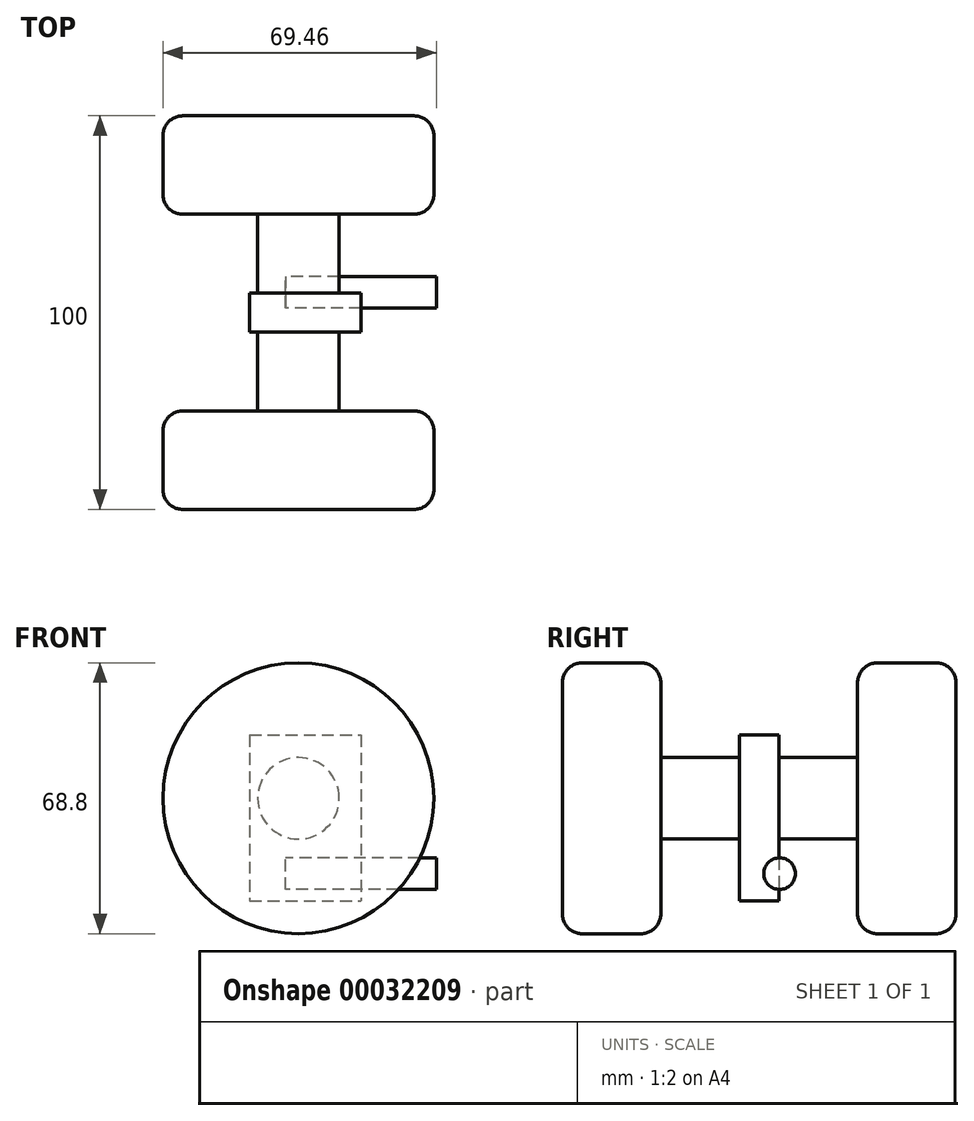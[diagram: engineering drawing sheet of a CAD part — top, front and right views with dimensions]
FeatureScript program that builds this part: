
annotation { "Feature Type Name" : "Feature", "Feature Type Description" : "" }
export const myFeature = defineFeature(function(context is Context, id is Id, definition is map)
    precondition{}
    {
        {
            var Q0;
            Q0=qCreatedBy(makeId("Front.planeOp"),FACE);
            var sketch = newSketch(context, id + "F0", { "sketchPlane" : qUnion([Q0])});
            skCircle(sketch, "E0", {"center": v(0, 0) * mm, "radius": 34.4 * mm});
            skSolve(sketch);
        }
        {
            var Q0;
            Q0=makeQuery(id+"F0.imprint","IMPRINT",FACE,{"disambiguationData":[TD([[makeQuery(id+"F0.imprint","IMPRINT",EDGE,{"derivedFrom":sQuery(id+"F0.wireOp",EDGE,"E0")}),1.0]])]});
            extrude(context, id + "F1", {"entities" : qUnion([Q0]), "depth" : 25 * mm});
        }
        {
            var Q0;
            Q0=makeQuery(id+"F1.opExtrude","CAP_FACE",FACE,{"disambiguationData":[OSD([sQuery(id+"F0.wireOp",EDGE,"E0")])],"isStart":true});
            var sketch = newSketch(context, id + "F2", { "sketchPlane" : qUnion([Q0])});
            skCircle(sketch, "E1", {"center": v(0, 0) * mm, "radius": 10.36 * mm});
            skSolve(sketch);
        }
        {
            var Q0;
            Q0 = qSketchRegion(id + "F2", true);
            extrude(context, id + "F3", {"entities" : qUnion([Q0]), "operationType" : NewBodyOperationType.ADD, "depth" : 25 * mm});
        }
        {
            var Q0;
            Q0=makeQuery(id+"F1.opExtrude","CAP_EDGE",EDGE,{"disambiguationData":[OSD([sQuery(id+"F0.wireOp",EDGE,"E0")])],"isStart":true});
            var Q1;
            Q1=makeQuery(id+"F1.opExtrude","CAP_EDGE",EDGE,{"disambiguationData":[OSD([sQuery(id+"F0.wireOp",EDGE,"E0")])],"isStart":false});
            fillet(context, id + "F4", {"entities" : qUnion([Q0, Q1]), "radius" : 5 * mm, "tangentPropagation" : true, "allowEdgeOverflow" : false});
        }
        {
            var Q0;
            Q0=makeQuery(id+"F3.opExtrude","CAP_FACE",FACE,{"disambiguationData":[OSD([sQuery(id+"F2.wireOp",EDGE,"E1")])],"isStart":false});
            var sketch = newSketch(context, id + "F5", { "sketchPlane" : qUnion([Q0])});
            skLineSegment(sketch, "E2.bottom", {"start": v(12.41, 16.07) * mm, "end": v(-15.9, 16.07) * mm});
            skLineSegment(sketch, "E2.top", {"start": v(12.41, -26.08) * mm, "end": v(-15.9, -26.08) * mm});
            skLineSegment(sketch, "E2.left", {"start": v(12.41, 16.07) * mm, "end": v(12.41, -26.08) * mm});
            skLineSegment(sketch, "E2.right", {"start": v(-15.9, 16.07) * mm, "end": v(-15.9, -26.08) * mm});
            skSolve(sketch);
        }
        {
            var Q0;
            Q0=makeQuery(id+"F5.imprint","IMPRINT",FACE,{"disambiguationData":[TD([[makeQuery(id+"F5.imprint","IMPRINT",EDGE,{"derivedFrom":sQuery(id+"F5.wireOp",EDGE,"E2.bottom")}),1.0]])]});
            extrude(context, id + "F6", {"entities" : qUnion([Q0]), "endBound" : BoundingType.SYMMETRIC, "depth" : 10 * mm});
        }
        {
            var Q0;
            Q0=makeQuery(id+"F6.opExtrude","SWEPT_FACE",FACE,{"disambiguationData":[OSD([sQuery(id+"F5.wireOp",EDGE,"E2.right")])]});
            var sketch = newSketch(context, id + "F7", { "sketchPlane" : qUnion([Q0])});
            skCircle(sketch, "E3", {"center": v(30.2, -19.15) * mm, "radius": 4 * mm});
            skSolve(sketch);
        }
        {
            var Q0;
            Q0 = qSketchRegion(id + "F7", true);
            var Q1;
            Q1=makeQuery(id+"F7.imprint","IMPRINT",FACE,{"disambiguationData":[TD([[makeQuery(id+"F7.imprint","IMPRINT",EDGE,{"derivedFrom":sQuery(id+"F7.wireOp",EDGE,"E3")}),1.0]])]});
            extrude(context, id + "F8", {"entities" : qUnion([Q0, Q1]), "endBound" : BoundingType.SYMMETRIC, "depth" : 38.3 * mm});
        }
        {
            var Q0;
            Q0=makeQuery(id+"F1.opExtrude","SWEPT_BODY",BODY,{"disambiguationData":[OSD([sQuery(id+"F0.wireOp",EDGE,"E0")])]});
            var Q1;
            Q1=makeQuery(id+"F3.opExtrude","CAP_FACE",FACE,{"disambiguationData":[OSD([sQuery(id+"F2.wireOp",EDGE,"E1")])],"isStart":false});
            mirror(context, id + "F9", {"operationType" : NewBodyOperationType.ADD, "entities" : qUnion([Q0]), "mirrorPlane" : qUnion([Q1])});
        }
    });
